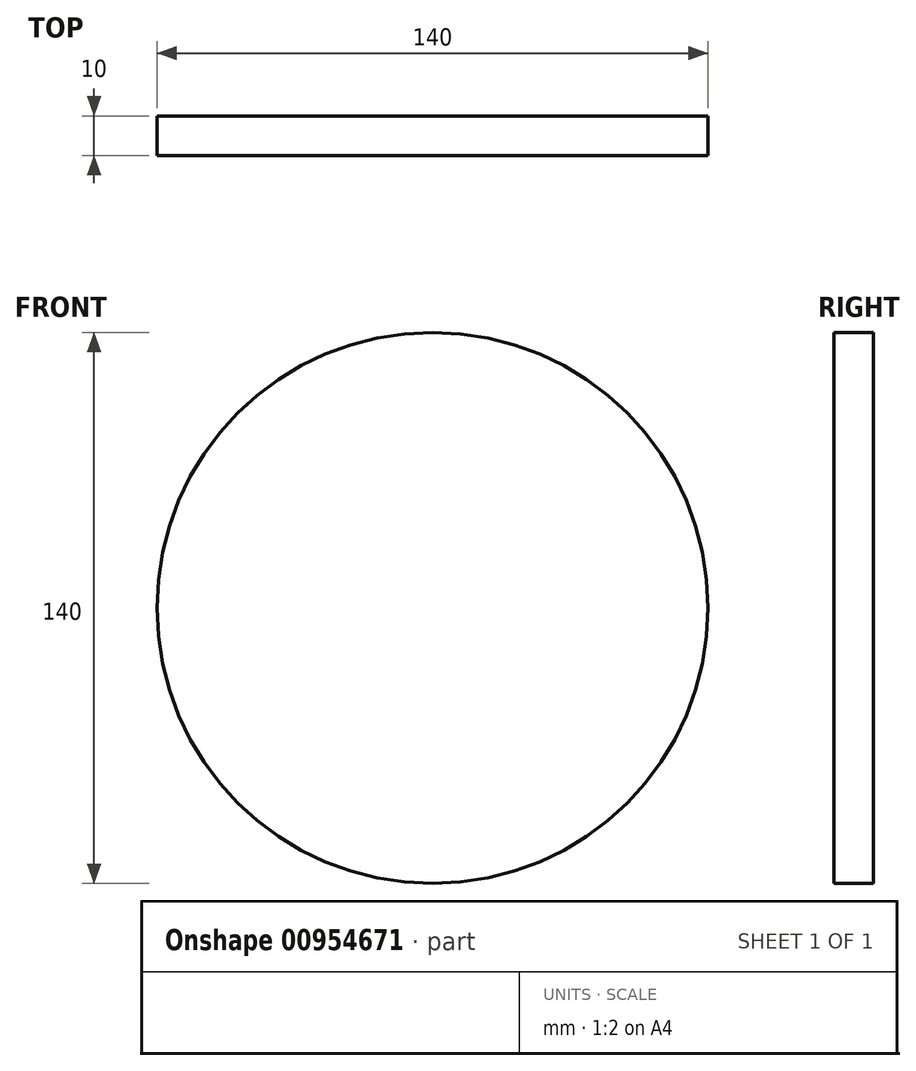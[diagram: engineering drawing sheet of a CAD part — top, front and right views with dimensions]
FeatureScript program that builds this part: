
annotation { "Feature Type Name" : "Feature", "Feature Type Description" : "" }
export const myFeature = defineFeature(function(context is Context, id is Id, definition is map)
    precondition{}
    {
        {
            var Q0;
            Q0=qCreatedBy(makeId("Front.planeOp"),FACE);
            var sketch = newSketch(context, id + "F0", { "sketchPlane" : qUnion([Q0])});
            skCircle(sketch, "E0", {"center": v(0, 0) * mm, "radius": 70 * mm});
            skSolve(sketch);
        }
        {
            var Q0;
            Q0 = qSketchRegion(id + "F0", true);
            extrude(context, id + "F1", {"entities" : qUnion([Q0]), "depth" : 10 * mm, "offsetDistance" : 25.4 * mm});
        }
    });
